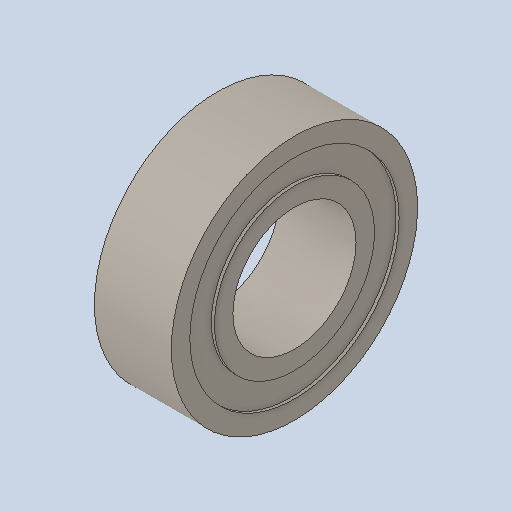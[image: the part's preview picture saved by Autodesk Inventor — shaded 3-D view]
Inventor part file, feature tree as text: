
AUTODESK INVENTOR PART (.ipt)
format: ipt  version: 2023 (Build 270158000, 158)  size: 126,976 bytes
history: native  units: in
note: dims shown in document units (in); Inventor stores cm internally (conversion verified against a paired STEP export)
features: revolve x1
ambient origin geometry x8: Origin, YZ Plane, XZ Plane, XY Plane, X Axis, Y Axis, Z Axis, Center Point
bodies: Solid1 (feature_tree)
feature tree (1):
  revolve  "Revolve1"  [1 undecoded]
note: 1 required parameter value undecoded (feature->parameter linkage not recoverable at this tier; creation-order binding heuristic only, values carry confidence <= 0.55)
